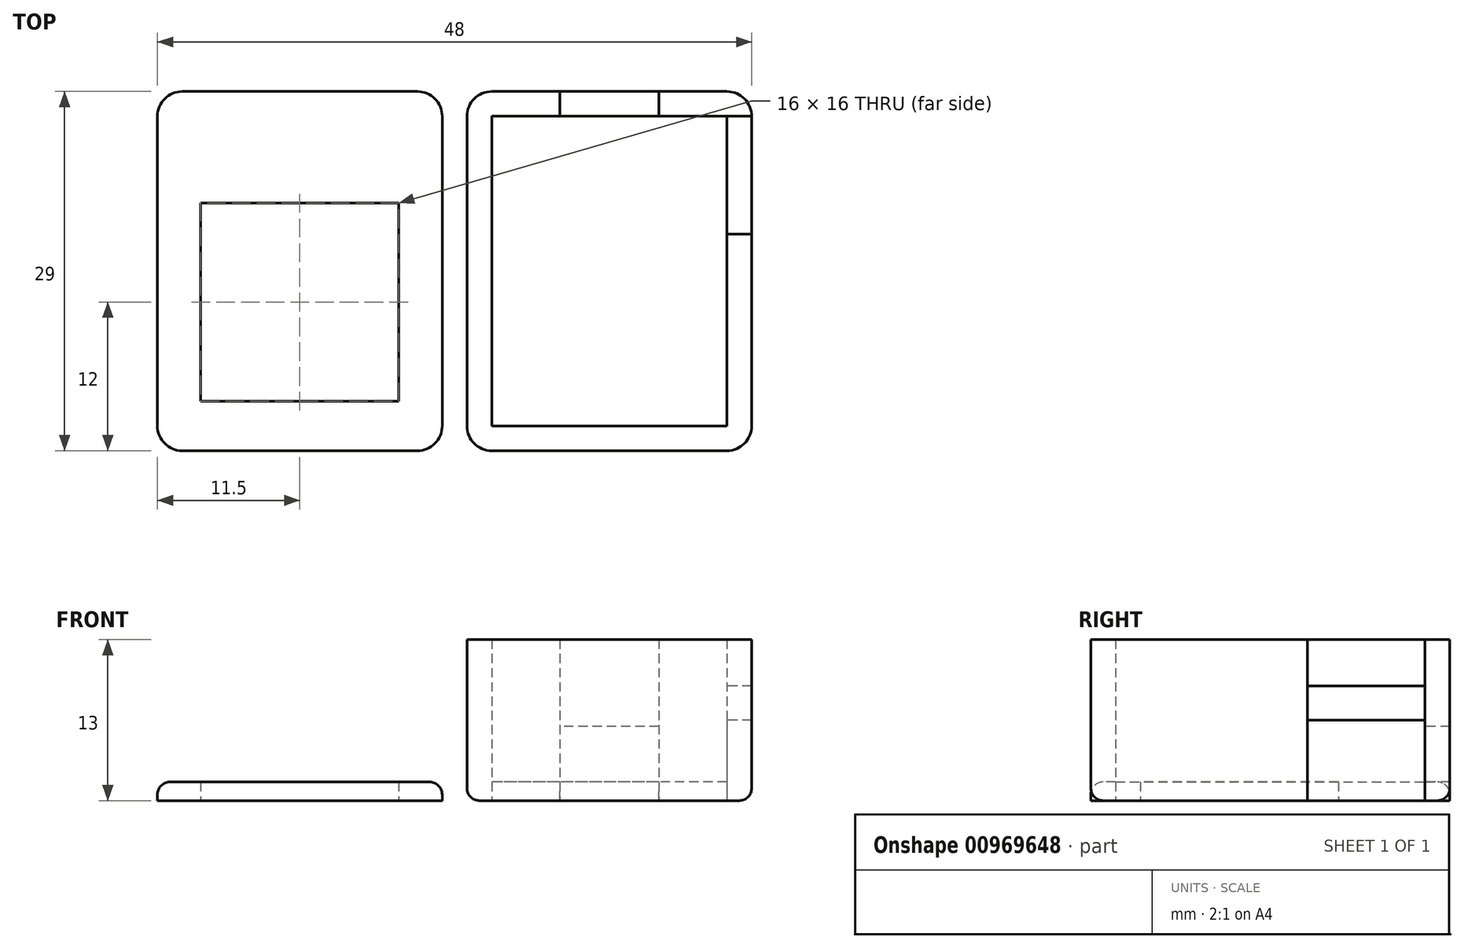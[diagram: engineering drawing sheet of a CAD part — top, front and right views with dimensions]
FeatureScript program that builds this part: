
annotation { "Feature Type Name" : "Feature", "Feature Type Description" : "" }
export const myFeature = defineFeature(function(context is Context, id is Id, definition is map)
    precondition{}
    {
        {
            var Q0;
            Q0=qCreatedBy(makeId("Top.planeOp"),FACE);
            var sketch = newSketch(context, id + "F0", { "sketchPlane" : qUnion([Q0])});
            skLineSegment(sketch, "E0.bottom", {"start": v(9.5, -12.5) * mm, "end": v(-9.5, -12.5) * mm});
            skLineSegment(sketch, "E0.top", {"start": v(9.5, 12.5) * mm, "end": v(-9.5, 12.5) * mm});
            skLineSegment(sketch, "E0.left", {"start": v(9.5, -12.5) * mm, "end": v(9.5, 12.5) * mm});
            skLineSegment(sketch, "E0.right", {"start": v(-9.5, -12.5) * mm, "end": v(-9.5, 12.5) * mm});
            skPoint(sketch, "E0.middle", {"position": v(0, 0) * mm});
            skLineSegment(sketch, "E1.0", {"start": v(11.5, -12.5) * mm, "end": v(11.5, 12.5) * mm});
            skLineSegment(sketch, "E1.1", {"start": v(9.5, -14.5) * mm, "end": v(-9.5, -14.5) * mm});
            skLineSegment(sketch, "E1.2", {"start": v(-11.5, -12.5) * mm, "end": v(-11.5, 12.5) * mm});
            skLineSegment(sketch, "E1.3", {"start": v(9.5, 14.5) * mm, "end": v(-9.5, 14.5) * mm});
            skLineSegment(sketch, "E2.bottom", {"start": v(-4, 14.5) * mm, "end": v(4, 14.5) * mm});
            skLineSegment(sketch, "E2.top", {"start": v(-4, 12.5) * mm, "end": v(4, 12.5) * mm});
            skLineSegment(sketch, "E2.left", {"start": v(-4, 14.5) * mm, "end": v(-4, 12.5) * mm});
            skLineSegment(sketch, "E2.right", {"start": v(4, 14.5) * mm, "end": v(4, 12.5) * mm});
            skPoint(sketch, "E3.visualSharp", {"position": v(-11.5, 14.5) * mm});
            skArc(sketch, "E3.filletArc", {"start": v(-9.5, 14.5) * mm, "mid": v(-10.91, 13.91) * mm, "end": v(-11.5, 12.5) * mm});
            skPoint(sketch, "E4.visualSharp", {"position": v(11.5, 14.5) * mm});
            skArc(sketch, "E4.filletArc", {"start": v(11.5, 12.5) * mm, "mid": v(10.91, 13.91) * mm, "end": v(9.5, 14.5) * mm});
            skPoint(sketch, "E5.visualSharp", {"position": v(11.5, -14.5) * mm});
            skArc(sketch, "E5.filletArc", {"start": v(9.5, -14.5) * mm, "mid": v(10.91, -13.91) * mm, "end": v(11.5, -12.5) * mm});
            skPoint(sketch, "E6.visualSharp", {"position": v(-11.5, -14.5) * mm});
            skArc(sketch, "E6.filletArc", {"start": v(-11.5, -12.5) * mm, "mid": v(-10.91, -13.91) * mm, "end": v(-9.5, -14.5) * mm});
            skLineSegment(sketch, "E7.bottom", {"start": v(-7.5, -12.5) * mm, "end": v(7.5, -12.5) * mm});
            skLineSegment(sketch, "E7.top", {"start": v(-7.5, -14.5) * mm, "end": v(7.5, -14.5) * mm});
            skLineSegment(sketch, "E7.left", {"start": v(-7.5, -12.5) * mm, "end": v(-7.5, -14.5) * mm});
            skLineSegment(sketch, "E7.right", {"start": v(7.5, -12.5) * mm, "end": v(7.5, -14.5) * mm});
            skLineSegment(sketch, "E8.bottom", {"start": v(-11.5, 12.5) * mm, "end": v(-9.5, 12.5) * mm});
            skLineSegment(sketch, "E8.top", {"start": v(-11.5, 3) * mm, "end": v(-9.5, 3) * mm});
            skLineSegment(sketch, "E8.left", {"start": v(-11.5, 12.5) * mm, "end": v(-11.5, 3) * mm});
            skLineSegment(sketch, "E8.right", {"start": v(-9.5, 12.5) * mm, "end": v(-9.5, 3) * mm});
            skLineSegment(sketch, "E9.bottom", {"start": v(11.5, 12.5) * mm, "end": v(9.5, 12.5) * mm});
            skLineSegment(sketch, "E9.top", {"start": v(11.5, 3) * mm, "end": v(9.5, 3) * mm});
            skLineSegment(sketch, "E9.left", {"start": v(11.5, 12.5) * mm, "end": v(11.5, 3) * mm});
            skLineSegment(sketch, "E9.right", {"start": v(9.5, 12.5) * mm, "end": v(9.5, 3) * mm});
            skSolve(sketch);
        }
        {
            var Q0;
            Q0=qCreatedBy(makeId("Top.planeOp"),FACE);
            var sketch = newSketch(context, id + "F1", { "sketchPlane" : qUnion([Q0])});
            skLineSegment(sketch, "E10.bottom", {"start": v(-15.5, -12.5) * mm, "end": v(-34.5, -12.5) * mm});
            skLineSegment(sketch, "E10.top", {"start": v(-15.5, 12.5) * mm, "end": v(-34.5, 12.5) * mm});
            skLineSegment(sketch, "E10.left", {"start": v(-15.5, -12.5) * mm, "end": v(-15.5, 12.5) * mm});
            skLineSegment(sketch, "E10.right", {"start": v(-34.5, -12.5) * mm, "end": v(-34.5, 12.5) * mm});
            skPoint(sketch, "E10.middle", {"position": v(-25, 0) * mm});
            skLineSegment(sketch, "E11.0", {"start": v(-13.5, -12.5) * mm, "end": v(-13.5, 12.5) * mm});
            skLineSegment(sketch, "E11.1", {"start": v(-15.5, -14.5) * mm, "end": v(-34.5, -14.5) * mm});
            skLineSegment(sketch, "E11.2", {"start": v(-36.5, -12.5) * mm, "end": v(-36.5, 12.5) * mm});
            skLineSegment(sketch, "E11.3", {"start": v(-15.5, 14.5) * mm, "end": v(-34.5, 14.5) * mm});
            skLineSegment(sketch, "E12.bottom", {"start": v(-29, 14.5) * mm, "end": v(-21, 14.5) * mm});
            skLineSegment(sketch, "E12.top", {"start": v(-29, 12.5) * mm, "end": v(-21, 12.5) * mm});
            skLineSegment(sketch, "E12.left", {"start": v(-29, 14.5) * mm, "end": v(-29, 12.5) * mm});
            skLineSegment(sketch, "E12.right", {"start": v(-21, 14.5) * mm, "end": v(-21, 12.5) * mm});
            skPoint(sketch, "E13.visualSharp", {"position": v(-36.5, 14.5) * mm});
            skArc(sketch, "E13.filletArc", {"start": v(-34.5, 14.5) * mm, "mid": v(-35.91, 13.91) * mm, "end": v(-36.5, 12.5) * mm});
            skPoint(sketch, "E14.visualSharp", {"position": v(-13.5, 14.5) * mm});
            skArc(sketch, "E14.filletArc", {"start": v(-13.5, 12.5) * mm, "mid": v(-14.09, 13.91) * mm, "end": v(-15.5, 14.5) * mm});
            skPoint(sketch, "E15.visualSharp", {"position": v(-13.5, -14.5) * mm});
            skArc(sketch, "E15.filletArc", {"start": v(-15.5, -14.5) * mm, "mid": v(-14.09, -13.91) * mm, "end": v(-13.5, -12.5) * mm});
            skPoint(sketch, "E16.visualSharp", {"position": v(-36.5, -14.5) * mm});
            skArc(sketch, "E16.filletArc", {"start": v(-36.5, -12.5) * mm, "mid": v(-35.91, -13.91) * mm, "end": v(-34.5, -14.5) * mm});
            skLineSegment(sketch, "E17.bottom", {"start": v(-32.5, -12.5) * mm, "end": v(-17.5, -12.5) * mm});
            skLineSegment(sketch, "E17.top", {"start": v(-32.5, -14.5) * mm, "end": v(-17.5, -14.5) * mm});
            skLineSegment(sketch, "E17.left", {"start": v(-32.5, -12.5) * mm, "end": v(-32.5, -14.5) * mm});
            skLineSegment(sketch, "E17.right", {"start": v(-17.5, -12.5) * mm, "end": v(-17.5, -14.5) * mm});
            skLineSegment(sketch, "E18.bottom", {"start": v(-36.5, 12.5) * mm, "end": v(-34.5, 12.5) * mm});
            skLineSegment(sketch, "E18.top", {"start": v(-36.5, 3) * mm, "end": v(-34.5, 3) * mm});
            skLineSegment(sketch, "E18.left", {"start": v(-36.5, 12.5) * mm, "end": v(-36.5, 3) * mm});
            skLineSegment(sketch, "E18.right", {"start": v(-34.5, 12.5) * mm, "end": v(-34.5, 3) * mm});
            skLineSegment(sketch, "E19.bottom", {"start": v(-13.5, 12.5) * mm, "end": v(-15.5, 12.5) * mm});
            skLineSegment(sketch, "E19.top", {"start": v(-13.5, 3) * mm, "end": v(-15.5, 3) * mm});
            skLineSegment(sketch, "E19.left", {"start": v(-13.5, 12.5) * mm, "end": v(-13.5, 3) * mm});
            skLineSegment(sketch, "E19.right", {"start": v(-15.5, 12.5) * mm, "end": v(-15.5, 3) * mm});
            skLineSegment(sketch, "E20.bottom", {"start": v(-33, 5.5) * mm, "end": v(-17, 5.5) * mm});
            skLineSegment(sketch, "E20.top", {"start": v(-33, -10.5) * mm, "end": v(-17, -10.5) * mm});
            skLineSegment(sketch, "E20.left", {"start": v(-33, 5.5) * mm, "end": v(-33, -10.5) * mm});
            skLineSegment(sketch, "E20.right", {"start": v(-17, 5.5) * mm, "end": v(-17, -10.5) * mm});
            skSolve(sketch);
        }
        {
            var Q0;
            {var subQ1=sQuery(id+"F0.wireOp",EDGE,"E2.left");Q0=makeQuery(id+"F0.imprint","IMPRINT",FACE,{"disambiguationData":[TD([[makeQuery(id+"F0.imprint","IMPRINT",EDGE,{"derivedFrom":subQ1}),-1.0]])]});}
            var Q1;
            {var subQ0=sQuery(id+"F0.wireOp",EDGE,"E8.bottom");Q1=makeQuery(id+"F0.imprint","IMPRINT",FACE,{"disambiguationData":[TD([[makeQuery(id+"F0.imprint","IMPRINT",EDGE,{"derivedFrom":subQ0}),-1.0]])]});}
            var Q2;
            {var subQ0=sQuery(id+"F0.wireOp",EDGE,"E6.filletArc");Q2=makeQuery(id+"F0.imprint","IMPRINT",FACE,{"disambiguationData":[TD([[makeQuery(id+"F0.imprint","IMPRINT",EDGE,{"derivedFrom":subQ0}),1.0]])]});}
            var Q3;
            {var subQ2=sQuery(id+"F0.wireOp",EDGE,"E7.left");Q3=makeQuery(id+"F0.imprint","IMPRINT",FACE,{"disambiguationData":[TD([[makeQuery(id+"F0.imprint","IMPRINT",EDGE,{"derivedFrom":subQ2}),1.0]])]});}
            var Q4;
            {var subQ2=sQuery(id+"F0.wireOp",EDGE,"E5.filletArc");Q4=makeQuery(id+"F0.imprint","IMPRINT",FACE,{"disambiguationData":[TD([[makeQuery(id+"F0.imprint","IMPRINT",EDGE,{"derivedFrom":subQ2}),1.0]])]});}
            var Q5;
            {var subQ0=sQuery(id+"F0.wireOp",EDGE,"E2.right");Q5=makeQuery(id+"F0.imprint","IMPRINT",FACE,{"disambiguationData":[TD([[makeQuery(id+"F0.imprint","IMPRINT",EDGE,{"derivedFrom":subQ0}),1.0]])]});}
            extrude(context, id + "F2", {"entities" : qUnion([Q0, Q1, Q2, Q3, Q4, Q5]), "depth" : 13 * mm, "offsetDistance" : 25 * mm});
        }
        {
            var Q0;
            Q0=qCreatedBy(makeId("Top.planeOp"),FACE);
            var sketch = newSketch(context, id + "F3", { "sketchPlane" : qUnion([Q0])});
            skLineSegment(sketch, "E21.bottom", {"start": v(9.5, -12.5) * mm, "end": v(-9.5, -12.5) * mm});
            skLineSegment(sketch, "E21.top", {"start": v(9.5, 12.5) * mm, "end": v(-9.5, 12.5) * mm});
            skLineSegment(sketch, "E21.left", {"start": v(9.5, -12.5) * mm, "end": v(9.5, 12.5) * mm});
            skLineSegment(sketch, "E21.right", {"start": v(-9.5, -12.5) * mm, "end": v(-9.5, 12.5) * mm});
            skPoint(sketch, "E21.middle", {"position": v(0, 0) * mm});
            skLineSegment(sketch, "E22.0", {"start": v(11.5, -12.5) * mm, "end": v(11.5, 12.5) * mm});
            skLineSegment(sketch, "E22.1", {"start": v(9.5, -14.5) * mm, "end": v(-9.5, -14.5) * mm});
            skLineSegment(sketch, "E22.2", {"start": v(-11.5, -12.5) * mm, "end": v(-11.5, 12.5) * mm});
            skLineSegment(sketch, "E22.3", {"start": v(9.5, 14.5) * mm, "end": v(-9.5, 14.5) * mm});
            skLineSegment(sketch, "E23.bottom", {"start": v(-4, 14.5) * mm, "end": v(4, 14.5) * mm});
            skLineSegment(sketch, "E23.top", {"start": v(-4, 12.5) * mm, "end": v(4, 12.5) * mm});
            skLineSegment(sketch, "E23.left", {"start": v(-4, 14.5) * mm, "end": v(-4, 12.5) * mm});
            skLineSegment(sketch, "E23.right", {"start": v(4, 14.5) * mm, "end": v(4, 12.5) * mm});
            skPoint(sketch, "E24.visualSharp", {"position": v(-11.5, 14.5) * mm});
            skArc(sketch, "E24.filletArc", {"start": v(-9.5, 14.5) * mm, "mid": v(-10.91, 13.91) * mm, "end": v(-11.5, 12.5) * mm});
            skPoint(sketch, "E25.visualSharp", {"position": v(11.5, 14.5) * mm});
            skArc(sketch, "E25.filletArc", {"start": v(11.5, 12.5) * mm, "mid": v(10.91, 13.91) * mm, "end": v(9.5, 14.5) * mm});
            skPoint(sketch, "E26.visualSharp", {"position": v(11.5, -14.5) * mm});
            skArc(sketch, "E26.filletArc", {"start": v(9.5, -14.5) * mm, "mid": v(10.91, -13.91) * mm, "end": v(11.5, -12.5) * mm});
            skPoint(sketch, "E27.visualSharp", {"position": v(-11.5, -14.5) * mm});
            skArc(sketch, "E27.filletArc", {"start": v(-11.5, -12.5) * mm, "mid": v(-10.91, -13.91) * mm, "end": v(-9.5, -14.5) * mm});
            skLineSegment(sketch, "E28.bottom", {"start": v(-7.5, -12.5) * mm, "end": v(7.5, -12.5) * mm});
            skLineSegment(sketch, "E28.top", {"start": v(-7.5, -14.5) * mm, "end": v(7.5, -14.5) * mm});
            skLineSegment(sketch, "E28.left", {"start": v(-7.5, -12.5) * mm, "end": v(-7.5, -14.5) * mm});
            skLineSegment(sketch, "E28.right", {"start": v(7.5, -12.5) * mm, "end": v(7.5, -14.5) * mm});
            skLineSegment(sketch, "E29.bottom", {"start": v(-11.5, 12.5) * mm, "end": v(-9.5, 12.5) * mm});
            skLineSegment(sketch, "E29.top", {"start": v(-11.5, 3) * mm, "end": v(-9.5, 3) * mm});
            skLineSegment(sketch, "E29.left", {"start": v(-11.5, 12.5) * mm, "end": v(-11.5, 3) * mm});
            skLineSegment(sketch, "E29.right", {"start": v(-9.5, 12.5) * mm, "end": v(-9.5, 3) * mm});
            skSolve(sketch);
        }
        {
            var Q0;
            {var subQ8=sQuery(id+"F3.wireOp",EDGE,"E21.left");Q0=makeQuery(id+"F3.imprint","IMPRINT",FACE,{"disambiguationData":[TD([[makeQuery(id+"F3.imprint","IMPRINT",EDGE,{"derivedFrom":subQ8}),1.0]])]});}
            var Q1;
            {var subQ2=sQuery(id+"F3.wireOp",EDGE,"E23.left");Q1=makeQuery(id+"F3.imprint","IMPRINT",FACE,{"disambiguationData":[TD([[makeQuery(id+"F3.imprint","IMPRINT",EDGE,{"derivedFrom":subQ2}),1.0]])]});}
            extrude(context, id + "F4", {"entities" : qUnion([Q0, Q1]), "depth" : 1.5 * mm, "offsetDistance" : 25 * mm});
        }
        {
            var Q0;
            Q0=qCreatedBy(makeId("Top.planeOp"),FACE);
            var sketch = newSketch(context, id + "F5", { "sketchPlane" : qUnion([Q0])});
            skLineSegment(sketch, "E30.bottom", {"start": v(9.5, -12.5) * mm, "end": v(-9.5, -12.5) * mm});
            skLineSegment(sketch, "E30.top", {"start": v(9.5, 12.5) * mm, "end": v(-9.5, 12.5) * mm});
            skLineSegment(sketch, "E30.left", {"start": v(9.5, -12.5) * mm, "end": v(9.5, 12.5) * mm});
            skLineSegment(sketch, "E30.right", {"start": v(-9.5, -12.5) * mm, "end": v(-9.5, 12.5) * mm});
            skPoint(sketch, "E30.middle", {"position": v(0, 0) * mm});
            skLineSegment(sketch, "E31.0", {"start": v(11.5, -12.5) * mm, "end": v(11.5, 12.5) * mm});
            skLineSegment(sketch, "E31.1", {"start": v(9.5, -14.5) * mm, "end": v(-9.5, -14.5) * mm});
            skLineSegment(sketch, "E31.2", {"start": v(-11.5, -12.5) * mm, "end": v(-11.5, 12.5) * mm});
            skLineSegment(sketch, "E31.3", {"start": v(9.5, 14.5) * mm, "end": v(-9.5, 14.5) * mm});
            skLineSegment(sketch, "E32.bottom", {"start": v(-4, 14.5) * mm, "end": v(4, 14.5) * mm});
            skLineSegment(sketch, "E32.top", {"start": v(-4, 12.5) * mm, "end": v(4, 12.5) * mm});
            skLineSegment(sketch, "E32.left", {"start": v(-4, 14.5) * mm, "end": v(-4, 12.5) * mm});
            skLineSegment(sketch, "E32.right", {"start": v(4, 14.5) * mm, "end": v(4, 12.5) * mm});
            skPoint(sketch, "E33.visualSharp", {"position": v(-11.5, 14.5) * mm});
            skArc(sketch, "E33.filletArc", {"start": v(-9.5, 14.5) * mm, "mid": v(-10.91, 13.91) * mm, "end": v(-11.5, 12.5) * mm});
            skPoint(sketch, "E34.visualSharp", {"position": v(11.5, 14.5) * mm});
            skArc(sketch, "E34.filletArc", {"start": v(11.5, 12.5) * mm, "mid": v(10.91, 13.91) * mm, "end": v(9.5, 14.5) * mm});
            skPoint(sketch, "E35.visualSharp", {"position": v(11.5, -14.5) * mm});
            skArc(sketch, "E35.filletArc", {"start": v(9.5, -14.5) * mm, "mid": v(10.91, -13.91) * mm, "end": v(11.5, -12.5) * mm});
            skPoint(sketch, "E36.visualSharp", {"position": v(-11.5, -14.5) * mm});
            skArc(sketch, "E36.filletArc", {"start": v(-11.5, -12.5) * mm, "mid": v(-10.91, -13.91) * mm, "end": v(-9.5, -14.5) * mm});
            skLineSegment(sketch, "E37.bottom", {"start": v(-7.5, -12.5) * mm, "end": v(7.5, -12.5) * mm});
            skLineSegment(sketch, "E37.top", {"start": v(-7.5, -14.5) * mm, "end": v(7.5, -14.5) * mm});
            skLineSegment(sketch, "E37.left", {"start": v(-7.5, -12.5) * mm, "end": v(-7.5, -14.5) * mm});
            skLineSegment(sketch, "E37.right", {"start": v(7.5, -12.5) * mm, "end": v(7.5, -14.5) * mm});
            skLineSegment(sketch, "E38.bottom", {"start": v(-11.5, 12.5) * mm, "end": v(-9.5, 12.5) * mm});
            skLineSegment(sketch, "E38.top", {"start": v(-11.5, 3) * mm, "end": v(-9.5, 3) * mm});
            skLineSegment(sketch, "E38.left", {"start": v(-11.5, 12.5) * mm, "end": v(-11.5, 3) * mm});
            skLineSegment(sketch, "E38.right", {"start": v(-9.5, 12.5) * mm, "end": v(-9.5, 3) * mm});
            skLineSegment(sketch, "E39.bottom", {"start": v(11.5, 12.5) * mm, "end": v(9.5, 12.5) * mm});
            skLineSegment(sketch, "E39.top", {"start": v(11.5, 3) * mm, "end": v(9.5, 3) * mm});
            skLineSegment(sketch, "E39.left", {"start": v(11.5, 12.5) * mm, "end": v(11.5, 3) * mm});
            skLineSegment(sketch, "E39.right", {"start": v(9.5, 12.5) * mm, "end": v(9.5, 3) * mm});
            skSolve(sketch);
        }
        {
            var Q0;
            {var subQ0=sQuery(id+"F5.wireOp",EDGE,"E39.bottom");Q0=makeQuery(id+"F5.imprint","IMPRINT",FACE,{"disambiguationData":[TD([[makeQuery(id+"F5.imprint","IMPRINT",EDGE,{"derivedFrom":subQ0}),1.0]])]});}
            extrude(context, id + "F6", {"entities" : qUnion([Q0]), "depth" : 6.5 * mm, "offsetDistance" : 25 * mm});
        }
        {
            var Q0;
            Q0=qCreatedBy(makeId("Top.planeOp"),FACE);
            var sketch = newSketch(context, id + "F7", { "sketchPlane" : qUnion([Q0])});
            skLineSegment(sketch, "E40.bottom", {"start": v(9.5, -12.5) * mm, "end": v(-9.5, -12.5) * mm});
            skLineSegment(sketch, "E40.top", {"start": v(9.5, 12.5) * mm, "end": v(-9.5, 12.5) * mm});
            skLineSegment(sketch, "E40.left", {"start": v(9.5, -12.5) * mm, "end": v(9.5, 12.5) * mm});
            skLineSegment(sketch, "E40.right", {"start": v(-9.5, -12.5) * mm, "end": v(-9.5, 12.5) * mm});
            skPoint(sketch, "E40.middle", {"position": v(0, 0) * mm});
            skLineSegment(sketch, "E41.0", {"start": v(11.5, -12.5) * mm, "end": v(11.5, 12.5) * mm});
            skLineSegment(sketch, "E41.1", {"start": v(9.5, -14.5) * mm, "end": v(-9.5, -14.5) * mm});
            skLineSegment(sketch, "E41.2", {"start": v(-11.5, -12.5) * mm, "end": v(-11.5, 12.5) * mm});
            skLineSegment(sketch, "E41.3", {"start": v(9.5, 14.5) * mm, "end": v(-9.5, 14.5) * mm});
            skLineSegment(sketch, "E42.bottom", {"start": v(-4, 14.5) * mm, "end": v(4, 14.5) * mm});
            skLineSegment(sketch, "E42.top", {"start": v(-4, 12.5) * mm, "end": v(4, 12.5) * mm});
            skLineSegment(sketch, "E42.left", {"start": v(-4, 14.5) * mm, "end": v(-4, 12.5) * mm});
            skLineSegment(sketch, "E42.right", {"start": v(4, 14.5) * mm, "end": v(4, 12.5) * mm});
            skPoint(sketch, "E43.visualSharp", {"position": v(-11.5, 14.5) * mm});
            skArc(sketch, "E43.filletArc", {"start": v(-9.5, 14.5) * mm, "mid": v(-10.91, 13.91) * mm, "end": v(-11.5, 12.5) * mm});
            skPoint(sketch, "E44.visualSharp", {"position": v(11.5, 14.5) * mm});
            skArc(sketch, "E44.filletArc", {"start": v(11.5, 12.5) * mm, "mid": v(10.91, 13.91) * mm, "end": v(9.5, 14.5) * mm});
            skPoint(sketch, "E45.visualSharp", {"position": v(11.5, -14.5) * mm});
            skArc(sketch, "E45.filletArc", {"start": v(9.5, -14.5) * mm, "mid": v(10.91, -13.91) * mm, "end": v(11.5, -12.5) * mm});
            skPoint(sketch, "E46.visualSharp", {"position": v(-11.5, -14.5) * mm});
            skArc(sketch, "E46.filletArc", {"start": v(-11.5, -12.5) * mm, "mid": v(-10.91, -13.91) * mm, "end": v(-9.5, -14.5) * mm});
            skLineSegment(sketch, "E47.bottom", {"start": v(-7.5, -12.5) * mm, "end": v(7.5, -12.5) * mm});
            skLineSegment(sketch, "E47.top", {"start": v(-7.5, -14.5) * mm, "end": v(7.5, -14.5) * mm});
            skLineSegment(sketch, "E47.left", {"start": v(-7.5, -12.5) * mm, "end": v(-7.5, -14.5) * mm});
            skLineSegment(sketch, "E47.right", {"start": v(7.5, -12.5) * mm, "end": v(7.5, -14.5) * mm});
            skLineSegment(sketch, "E48.bottom", {"start": v(-11.5, 12.5) * mm, "end": v(-9.5, 12.5) * mm});
            skLineSegment(sketch, "E48.top", {"start": v(-11.5, 3) * mm, "end": v(-9.5, 3) * mm});
            skLineSegment(sketch, "E48.left", {"start": v(-11.5, 12.5) * mm, "end": v(-11.5, 3) * mm});
            skLineSegment(sketch, "E48.right", {"start": v(-9.5, 12.5) * mm, "end": v(-9.5, 3) * mm});
            skLineSegment(sketch, "E49.bottom", {"start": v(11.5, 12.5) * mm, "end": v(9.5, 12.5) * mm});
            skLineSegment(sketch, "E49.top", {"start": v(11.5, 3) * mm, "end": v(9.5, 3) * mm});
            skLineSegment(sketch, "E49.left", {"start": v(11.5, 12.5) * mm, "end": v(11.5, 3) * mm});
            skLineSegment(sketch, "E49.right", {"start": v(9.5, 12.5) * mm, "end": v(9.5, 3) * mm});
            skSolve(sketch);
        }
        {
            var Q0;
            {var subQ2=sQuery(id+"F7.wireOp",EDGE,"E42.left");Q0=makeQuery(id+"F7.imprint","IMPRINT",FACE,{"disambiguationData":[TD([[makeQuery(id+"F7.imprint","IMPRINT",EDGE,{"derivedFrom":subQ2}),1.0]])]});}
            extrude(context, id + "F8", {"entities" : qUnion([Q0]), "depth" : 13 * mm, "offsetDistance" : 25 * mm, "hasSecondDirection" : true, "secondDirectionOppositeDirection" : false, "secondDirectionDepth" : 6 * mm});
        }
        {
            var Q0;
            Q0=qCreatedBy(makeId("Top.planeOp"),FACE);
            var sketch = newSketch(context, id + "F9", { "sketchPlane" : qUnion([Q0])});
            skLineSegment(sketch, "E50.bottom", {"start": v(9.5, -12.5) * mm, "end": v(-9.5, -12.5) * mm});
            skLineSegment(sketch, "E50.top", {"start": v(9.5, 12.5) * mm, "end": v(-9.5, 12.5) * mm});
            skLineSegment(sketch, "E50.left", {"start": v(9.5, -12.5) * mm, "end": v(9.5, 12.5) * mm});
            skLineSegment(sketch, "E50.right", {"start": v(-9.5, -12.5) * mm, "end": v(-9.5, 12.5) * mm});
            skPoint(sketch, "E50.middle", {"position": v(0, 0) * mm});
            skLineSegment(sketch, "E51.0", {"start": v(11.5, -12.5) * mm, "end": v(11.5, 12.5) * mm});
            skLineSegment(sketch, "E51.1", {"start": v(9.5, -14.5) * mm, "end": v(-9.5, -14.5) * mm});
            skLineSegment(sketch, "E51.2", {"start": v(-11.5, -12.5) * mm, "end": v(-11.5, 12.5) * mm});
            skLineSegment(sketch, "E51.3", {"start": v(9.5, 14.5) * mm, "end": v(-9.5, 14.5) * mm});
            skLineSegment(sketch, "E52.bottom", {"start": v(-4, 14.5) * mm, "end": v(4, 14.5) * mm});
            skLineSegment(sketch, "E52.top", {"start": v(-4, 12.5) * mm, "end": v(4, 12.5) * mm});
            skLineSegment(sketch, "E52.left", {"start": v(-4, 14.5) * mm, "end": v(-4, 12.5) * mm});
            skLineSegment(sketch, "E52.right", {"start": v(4, 14.5) * mm, "end": v(4, 12.5) * mm});
            skPoint(sketch, "E53.visualSharp", {"position": v(-11.5, 14.5) * mm});
            skArc(sketch, "E53.filletArc", {"start": v(-9.5, 14.5) * mm, "mid": v(-10.91, 13.91) * mm, "end": v(-11.5, 12.5) * mm});
            skPoint(sketch, "E54.visualSharp", {"position": v(11.5, 14.5) * mm});
            skArc(sketch, "E54.filletArc", {"start": v(11.5, 12.5) * mm, "mid": v(10.91, 13.91) * mm, "end": v(9.5, 14.5) * mm});
            skPoint(sketch, "E55.visualSharp", {"position": v(11.5, -14.5) * mm});
            skArc(sketch, "E55.filletArc", {"start": v(9.5, -14.5) * mm, "mid": v(10.91, -13.91) * mm, "end": v(11.5, -12.5) * mm});
            skPoint(sketch, "E56.visualSharp", {"position": v(-11.5, -14.5) * mm});
            skArc(sketch, "E56.filletArc", {"start": v(-11.5, -12.5) * mm, "mid": v(-10.91, -13.91) * mm, "end": v(-9.5, -14.5) * mm});
            skLineSegment(sketch, "E57.bottom", {"start": v(-7.5, -12.5) * mm, "end": v(7.5, -12.5) * mm});
            skLineSegment(sketch, "E57.top", {"start": v(-7.5, -14.5) * mm, "end": v(7.5, -14.5) * mm});
            skLineSegment(sketch, "E57.left", {"start": v(-7.5, -12.5) * mm, "end": v(-7.5, -14.5) * mm});
            skLineSegment(sketch, "E57.right", {"start": v(7.5, -12.5) * mm, "end": v(7.5, -14.5) * mm});
            skLineSegment(sketch, "E58.bottom", {"start": v(-11.5, 12.5) * mm, "end": v(-9.5, 12.5) * mm});
            skLineSegment(sketch, "E58.top", {"start": v(-11.5, 3) * mm, "end": v(-9.5, 3) * mm});
            skLineSegment(sketch, "E58.left", {"start": v(-11.5, 12.5) * mm, "end": v(-11.5, 3) * mm});
            skLineSegment(sketch, "E58.right", {"start": v(-9.5, 12.5) * mm, "end": v(-9.5, 3) * mm});
            skLineSegment(sketch, "E59.bottom", {"start": v(11.5, 12.5) * mm, "end": v(9.5, 12.5) * mm});
            skLineSegment(sketch, "E59.top", {"start": v(11.5, 3) * mm, "end": v(9.5, 3) * mm});
            skLineSegment(sketch, "E59.left", {"start": v(11.5, 12.5) * mm, "end": v(11.5, 3) * mm});
            skLineSegment(sketch, "E59.right", {"start": v(9.5, 12.5) * mm, "end": v(9.5, 3) * mm});
            skSolve(sketch);
        }
        {
            var Q0;
            {var subQ0=sQuery(id+"F9.wireOp",EDGE,"E59.bottom");Q0=makeQuery(id+"F9.imprint","IMPRINT",FACE,{"disambiguationData":[TD([[makeQuery(id+"F9.imprint","IMPRINT",EDGE,{"derivedFrom":subQ0}),1.0]])]});}
            extrude(context, id + "F10", {"entities" : qUnion([Q0]), "depth" : 13 * mm, "offsetDistance" : 25 * mm, "hasSecondDirection" : true, "secondDirectionOppositeDirection" : false, "secondDirectionDepth" : 9.25 * mm});
        }
        {
            var Q0;
            Q0=makeQuery(id+"F2.opExtrude","CAP_EDGE",EDGE,{"disambiguationData":[OSD([sQuery(id+"F0.wireOp",EDGE,"E1.1")])],"isStart":true});
            var Q1;
            {var subQ0=sQuery(id+"F0.wireOp",EDGE,"E1.3");Q1=makeQuery(id+"F2.opExtrude","CAP_EDGE",EDGE,{"disambiguationData":[OSD([subQ0]),TDD([makeQuery(id+"F0.imprint","IMPRINT",EDGE,{"disambiguationData":[TD([[makeQuery(id+"F0.imprint","INTERSECT",VERTEX,{"derivedFrom":[subQ0,sQuery(id+"F0.wireOp",EDGE,"E2.right")]}),1.0]])],"derivedFrom":subQ0})])],"isStart":true});}
            var Q2;
            Q2=makeQuery(id+"F6.opExtrude","CAP_EDGE",EDGE,{"disambiguationData":[OSD([sQuery(id+"F5.wireOp",EDGE,"E31.0")])],"isStart":true});
            var Q3;
            Q3=makeQuery(id+"F4.opExtrude","CAP_EDGE",EDGE,{"disambiguationData":[OSD([sQuery(id+"F3.wireOp",EDGE,"E22.3")])],"isStart":true});
            fillet(context, id + "F11", {"entities" : qUnion([Q0, Q1, Q2, Q3]), "radius" : 1 * mm, "tangentPropagation" : true, "allowEdgeOverflow" : false});
        }
        {
            var Q0;
            {var subQ2=sQuery(id+"F1.wireOp",EDGE,"E12.left");Q0=makeQuery(id+"F1.imprint","IMPRINT",FACE,{"disambiguationData":[TD([[makeQuery(id+"F1.imprint","IMPRINT",EDGE,{"derivedFrom":subQ2}),1.0]])]});}
            var Q1;
            {var subQ1=sQuery(id+"F1.wireOp",EDGE,"E12.left");Q1=makeQuery(id+"F1.imprint","IMPRINT",FACE,{"disambiguationData":[TD([[makeQuery(id+"F1.imprint","IMPRINT",EDGE,{"derivedFrom":subQ1}),-1.0]])]});}
            var Q2;
            {var subQ0=sQuery(id+"F1.wireOp",EDGE,"E18.bottom");Q2=makeQuery(id+"F1.imprint","IMPRINT",FACE,{"disambiguationData":[TD([[makeQuery(id+"F1.imprint","IMPRINT",EDGE,{"derivedFrom":subQ0}),-1.0]])]});}
            var Q3;
            {var subQ0=sQuery(id+"F1.wireOp",EDGE,"E16.filletArc");Q3=makeQuery(id+"F1.imprint","IMPRINT",FACE,{"disambiguationData":[TD([[makeQuery(id+"F1.imprint","IMPRINT",EDGE,{"derivedFrom":subQ0}),1.0]])]});}
            var Q4;
            {var subQ2=sQuery(id+"F1.wireOp",EDGE,"E17.left");Q4=makeQuery(id+"F1.imprint","IMPRINT",FACE,{"disambiguationData":[TD([[makeQuery(id+"F1.imprint","IMPRINT",EDGE,{"derivedFrom":subQ2}),1.0]])]});}
            var Q5;
            {var subQ2=sQuery(id+"F1.wireOp",EDGE,"E15.filletArc");Q5=makeQuery(id+"F1.imprint","IMPRINT",FACE,{"disambiguationData":[TD([[makeQuery(id+"F1.imprint","IMPRINT",EDGE,{"derivedFrom":subQ2}),1.0]])]});}
            var Q6;
            {var subQ0=sQuery(id+"F1.wireOp",EDGE,"E19.bottom");Q6=makeQuery(id+"F1.imprint","IMPRINT",FACE,{"disambiguationData":[TD([[makeQuery(id+"F1.imprint","IMPRINT",EDGE,{"derivedFrom":subQ0}),1.0]])]});}
            var Q7;
            {var subQ1=sQuery(id+"F1.wireOp",EDGE,"E12.right");Q7=makeQuery(id+"F1.imprint","IMPRINT",FACE,{"disambiguationData":[TD([[makeQuery(id+"F1.imprint","IMPRINT",EDGE,{"derivedFrom":subQ1}),1.0]])]});}
            var Q8;
            Q8=makeQuery(id+"F1.imprint","IMPRINT",FACE,{"disambiguationData":[TD([[makeQuery(id+"F1.imprint","IMPRINT",EDGE,{"derivedFrom":sQuery(id+"F1.wireOp",EDGE,"E20.bottom")}),1.0]])]});
            extrude(context, id + "F12", {"entities" : qUnion([Q0, Q1, Q2, Q3, Q4, Q5, Q6, Q7, Q8]), "depth" : 1.5 * mm, "offsetDistance" : 25 * mm});
        }
        {
            var Q0;
            Q0=makeQuery(id+"F12.opExtrude","CAP_EDGE",EDGE,{"disambiguationData":[OSD([sQuery(id+"F1.wireOp",EDGE,"E11.2")])],"isStart":false});
            fillet(context, id + "F13", {"entities" : qUnion([Q0]), "radius" : 1 * mm, "tangentPropagation" : true, "allowEdgeOverflow" : false});
        }
    });
